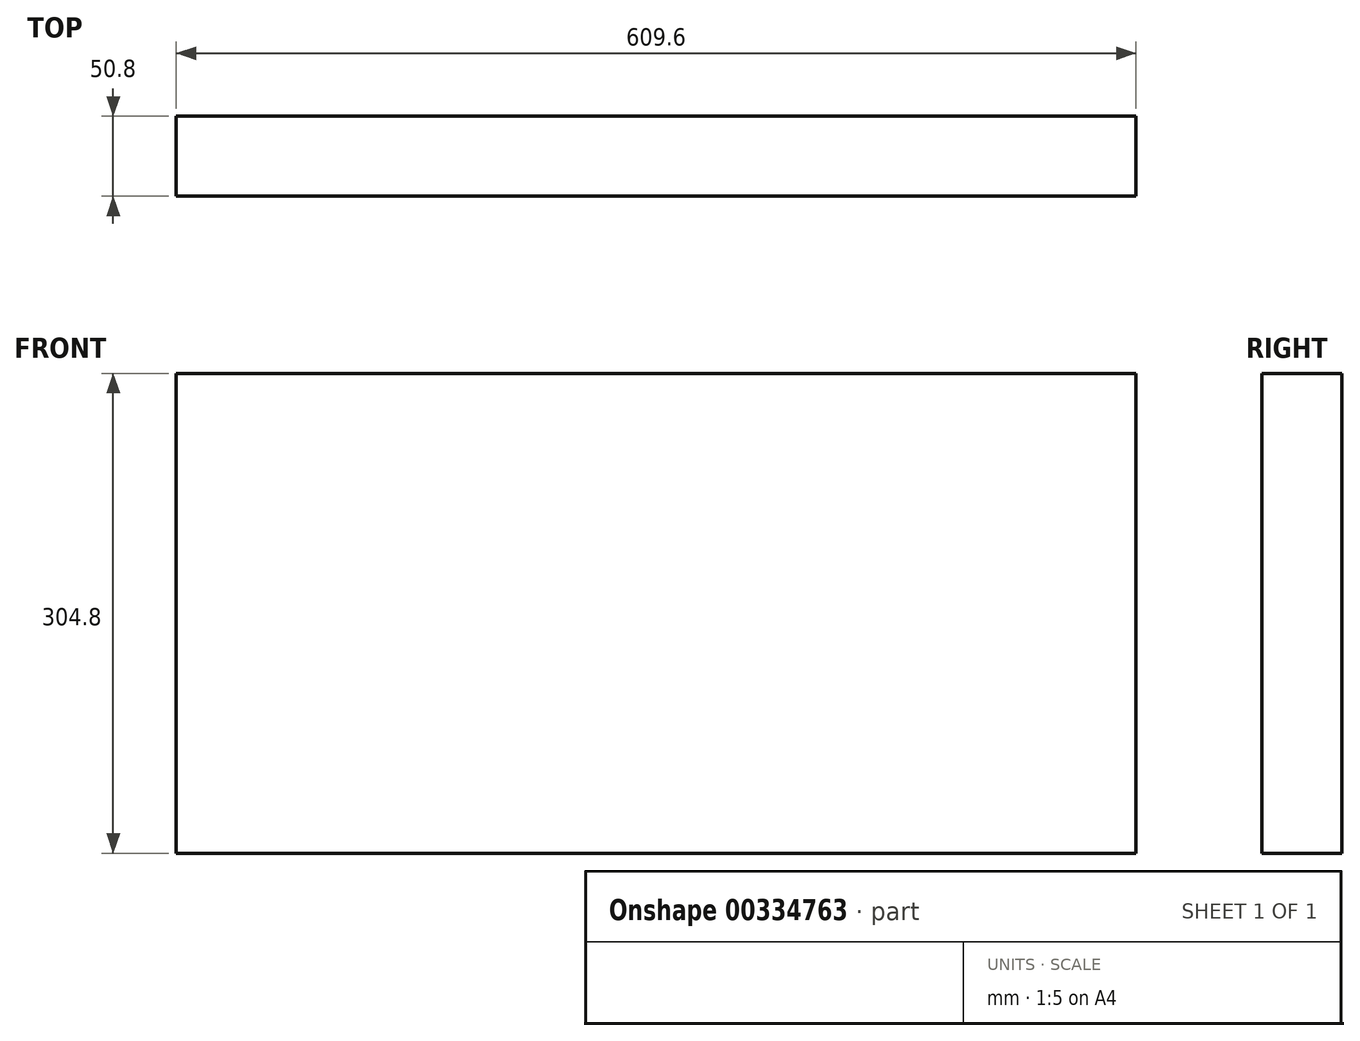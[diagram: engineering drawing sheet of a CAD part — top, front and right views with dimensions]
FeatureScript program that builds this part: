
annotation { "Feature Type Name" : "Feature", "Feature Type Description" : "" }
export const myFeature = defineFeature(function(context is Context, id is Id, definition is map)
    precondition{}
    {
        {
            var Q0;
            Q0=qCreatedBy(makeId("Front.planeOp"),FACE);
            var sketch = newSketch(context, id + "F0", { "sketchPlane" : qUnion([Q0])});
            skLineSegment(sketch, "E0.bottom", {"start": v(0, 0) * mm, "end": v(609.6, 0) * mm});
            skLineSegment(sketch, "E0.top", {"start": v(0, 304.8) * mm, "end": v(609.6, 304.8) * mm});
            skLineSegment(sketch, "E0.left", {"start": v(0, 0) * mm, "end": v(0, 304.8) * mm});
            skLineSegment(sketch, "E0.right", {"start": v(609.6, 0) * mm, "end": v(609.6, 304.8) * mm});
            skSolve(sketch);
        }
        {
            var Q0;
            Q0=qSketchRegion(id+"F0",true);
            extrude(context, id + "F1", {"entities" : qUnion([Q0]), "depth" : 50.8 * mm});
        }
    });
